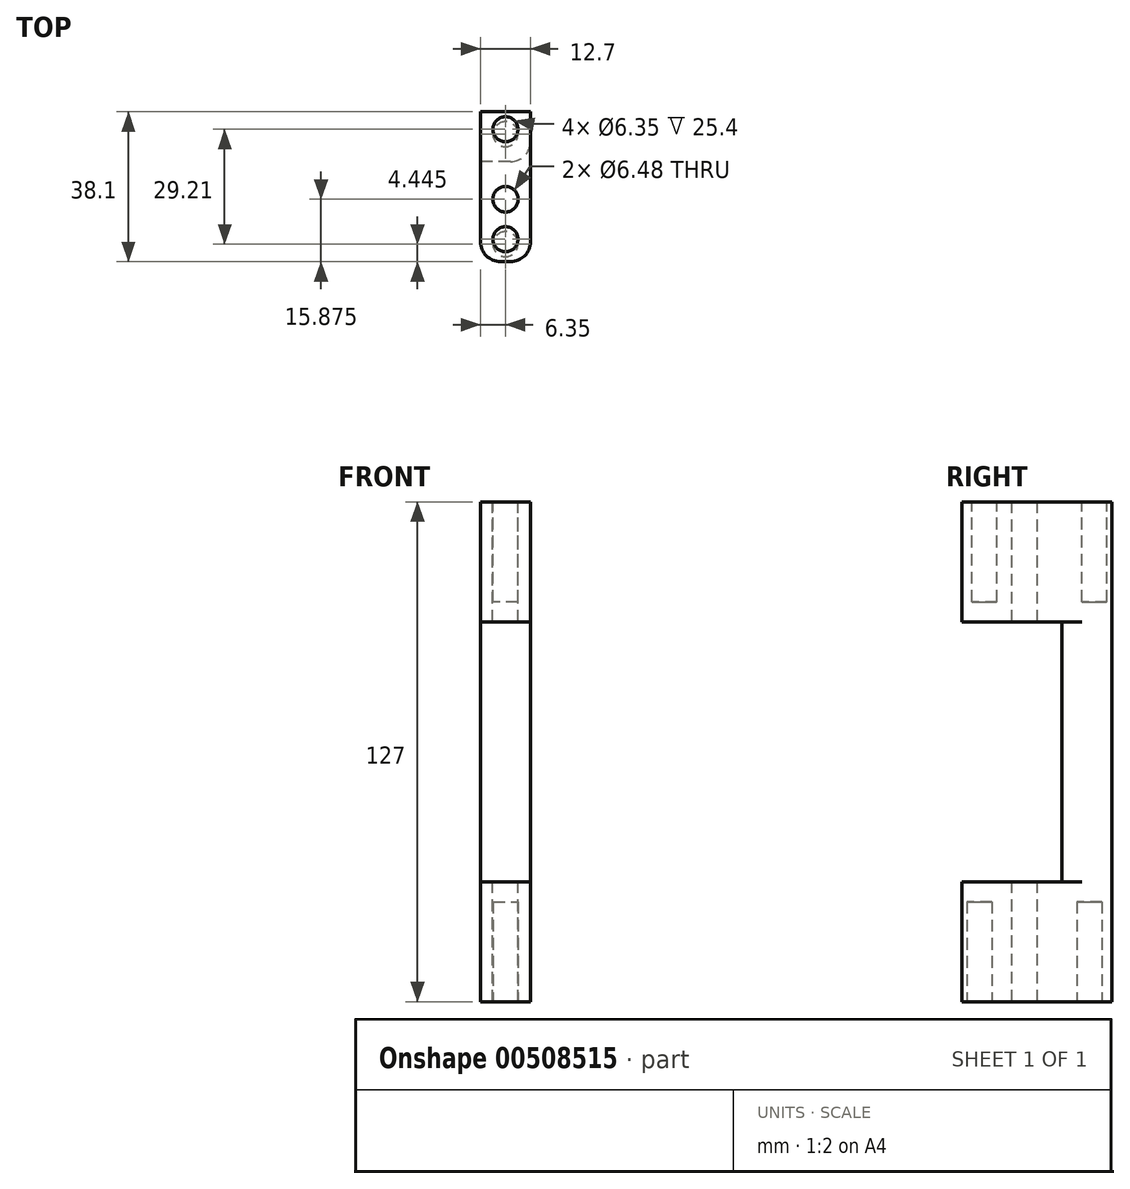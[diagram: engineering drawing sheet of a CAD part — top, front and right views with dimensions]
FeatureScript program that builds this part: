
annotation { "Feature Type Name" : "Feature", "Feature Type Description" : "" }
export const myFeature = defineFeature(function(context is Context, id is Id, definition is map)
    precondition{}
    {
        {
            var Q0;
            Q0=qCreatedBy(makeId("Top.planeOp"),FACE);
            var sketch = newSketch(context, id + "F0", { "sketchPlane" : qUnion([Q0])});
            skLineSegment(sketch, "E0.bottom", {"start": v(0, 0) * mm, "end": v(12.7, 0) * mm});
            skLineSegment(sketch, "E0.top", {"start": v(0, 38.1) * mm, "end": v(12.7, 38.1) * mm});
            skLineSegment(sketch, "E0.left", {"start": v(0, 0) * mm, "end": v(0, 38.1) * mm});
            skLineSegment(sketch, "E0.right", {"start": v(12.7, 0) * mm, "end": v(12.7, 38.1) * mm});
            skSolve(sketch);
        }
        {
            var Q0;
            Q0=makeQuery(id+"F0.imprint","IMPRINT",FACE,{"disambiguationData":[TD([[makeQuery(id+"F0.imprint","IMPRINT",EDGE,{"derivedFrom":sQuery(id+"F0.wireOp",EDGE,"E0.bottom")}),1.0]])]});
            extrude(context, id + "F1", {"entities" : qUnion([Q0]), "depth" : 127 * mm, "offsetDistance" : 25.4 * mm});
        }
        {
            var Q0;
            Q0=makeQuery(id+"F1.opExtrude","CAP_FACE",FACE,{"disambiguationData":[OSD([sQuery(id+"F0.wireOp",EDGE,"E0.bottom"),sQuery(id+"F0.wireOp",EDGE,"E0.top"),sQuery(id+"F0.wireOp",EDGE,"E0.left"),sQuery(id+"F0.wireOp",EDGE,"E0.right")])],"isStart":false});
            var sketch = newSketch(context, id + "F2", { "sketchPlane" : qUnion([Q0])});
            skCircle(sketch, "E1", {"center": v(6.35, 33.66) * mm, "radius": 3.18 * mm});
            skCircle(sketch, "E2", {"center": v(6.35, 5.71) * mm, "radius": 3.18 * mm});
            skLineSegment(sketch, "E3", {"start": v(0, 33.66) * mm, "end": v(12.7, 33.66) * mm, "construction": true});
            skLineSegment(sketch, "E4", {"start": v(0, 5.71) * mm, "end": v(12.7, 5.71) * mm, "construction": true});
            skLineSegment(sketch, "E5", {"start": v(0, 15.88) * mm, "end": v(12.7, 15.88) * mm, "construction": true});
            skCircle(sketch, "E6", {"center": v(6.35, 15.88) * mm, "radius": 3.24 * mm});
            skSolve(sketch);
        }
        {
            var Q0;
            Q0=makeQuery(id+"F2.imprint","IMPRINT",FACE,{"disambiguationData":[TD([[makeQuery(id+"F2.imprint","IMPRINT",EDGE,{"derivedFrom":sQuery(id+"F2.wireOp",EDGE,"E6")}),1.0]])]});
            extrude(context, id + "F3", {"entities" : qUnion([Q0]), "operationType" : NewBodyOperationType.REMOVE, "oppositeDirection" : true, "depth" : 152.4 * mm, "offsetDistance" : 25.4 * mm});
        }
        {
            var Q0;
            Q0=makeQuery(id+"F2.imprint","IMPRINT",FACE,{"disambiguationData":[TD([[makeQuery(id+"F2.imprint","IMPRINT",EDGE,{"derivedFrom":sQuery(id+"F2.wireOp",EDGE,"E1")}),1.0]])]});
            var Q1;
            Q1=makeQuery(id+"F2.imprint","IMPRINT",FACE,{"disambiguationData":[TD([[makeQuery(id+"F2.imprint","IMPRINT",EDGE,{"derivedFrom":sQuery(id+"F2.wireOp",EDGE,"E2")}),1.0]])]});
            extrude(context, id + "F4", {"entities" : qUnion([Q0, Q1]), "operationType" : NewBodyOperationType.REMOVE, "oppositeDirection" : true, "depth" : 25.4 * mm, "offsetDistance" : 25.4 * mm});
        }
        {
            var Q0;
            Q0=makeQuery(id+"F1.opExtrude","CAP_FACE",FACE,{"disambiguationData":[OSD([sQuery(id+"F0.wireOp",EDGE,"E0.bottom"),sQuery(id+"F0.wireOp",EDGE,"E0.top"),sQuery(id+"F0.wireOp",EDGE,"E0.left"),sQuery(id+"F0.wireOp",EDGE,"E0.right")])],"isStart":true});
            var sketch = newSketch(context, id + "F5", { "sketchPlane" : qUnion([Q0])});
            skCircle(sketch, "E7", {"center": v(6.35, -4.45) * mm, "radius": 3.18 * mm});
            skCircle(sketch, "E8", {"center": v(6.35, -32.39) * mm, "radius": 3.18 * mm});
            skLineSegment(sketch, "E9", {"start": v(0, -4.45) * mm, "end": v(12.7, -4.44) * mm, "construction": true});
            skLineSegment(sketch, "E10", {"start": v(0, -32.39) * mm, "end": v(12.7, -32.39) * mm, "construction": true});
            skSolve(sketch);
        }
        {
            var Q0;
            Q0=makeQuery(id+"F5.imprint","IMPRINT",FACE,{"disambiguationData":[TD([[makeQuery(id+"F5.imprint","IMPRINT",EDGE,{"derivedFrom":sQuery(id+"F5.wireOp",EDGE,"E7")}),1.0]])]});
            var Q1;
            Q1=makeQuery(id+"F5.imprint","IMPRINT",FACE,{"disambiguationData":[TD([[makeQuery(id+"F5.imprint","IMPRINT",EDGE,{"derivedFrom":sQuery(id+"F5.wireOp",EDGE,"E8")}),1.0]])]});
            extrude(context, id + "F6", {"entities" : qUnion([Q0, Q1]), "operationType" : NewBodyOperationType.REMOVE, "oppositeDirection" : true, "depth" : 25.4 * mm, "offsetDistance" : 25.4 * mm});
        }
        {
            var Q0;
            Q0=makeQuery(id+"F1.opExtrude","SWEPT_FACE",FACE,{"disambiguationData":[OSD([sQuery(id+"F0.wireOp",EDGE,"E0.left")])]});
            var sketch = newSketch(context, id + "F7", { "sketchPlane" : qUnion([Q0])});
            skLineSegment(sketch, "E11", {"start": v(0, 30.48) * mm, "end": v(-25.4, 30.48) * mm});
            skLineSegment(sketch, "E12", {"start": v(-25.4, 30.48) * mm, "end": v(-25.4, 96.52) * mm});
            skLineSegment(sketch, "E13", {"start": v(-25.4, 96.52) * mm, "end": v(0, 96.52) * mm});
            skSolve(sketch);
        }
        {
            var Q0;
            {var subQ0=sQuery(id+"F7.wireOp",EDGE,"E11");Q0=makeQuery(id+"F7.imprint","IMPRINT",FACE,{"disambiguationData":[TD([[makeQuery(id+"F7.imprint","IMPRINT",EDGE,{"derivedFrom":subQ0}),-1.0]])]});}
            extrude(context, id + "F8", {"entities" : qUnion([Q0]), "operationType" : NewBodyOperationType.REMOVE, "oppositeDirection" : true, "depth" : 25.4 * mm, "offsetDistance" : 25.4 * mm});
        }
        {
            var Q0;
            {var subQ0=sQuery(id+"F0.wireOp",EDGE,"E0.bottom");var subQ1=sQuery(id+"F0.wireOp",EDGE,"E0.right");Q0=makeQuery(id+"F8.boolean.opBoolean","SPLIT",EDGE,{"disambiguationData":[TD([makeQuery(id+"F8.opExtrude","SWEPT_FACE",FACE,{"disambiguationData":[OSD([sQuery(id+"F7.wireOp",EDGE,"E13")])]})])],"derivedFrom":makeQuery(id+"F1.opExtrude","SWEPT_EDGE",EDGE,{"disambiguationData":[OSD([subQ0,subQ1])]})});}
            var Q1;
            {var subQ0=sQuery(id+"F0.wireOp",EDGE,"E0.bottom");var subQ1=sQuery(id+"F0.wireOp",EDGE,"E0.left");Q1=makeQuery(id+"F8.boolean.opBoolean","SPLIT",EDGE,{"disambiguationData":[TD([makeQuery(id+"F8.opExtrude","SWEPT_FACE",FACE,{"disambiguationData":[OSD([sQuery(id+"F7.wireOp",EDGE,"E13")])]})])],"derivedFrom":makeQuery(id+"F1.opExtrude","SWEPT_EDGE",EDGE,{"disambiguationData":[OSD([subQ0,subQ1])]})});}
            var Q2;
            Q2=makeQuery(id+"F8.boolean.opBoolean","INTERSECT",EDGE,{"derivedFrom":[makeQuery(id+"F1.opExtrude","SWEPT_FACE",FACE,{"disambiguationData":[OSD([sQuery(id+"F0.wireOp",EDGE,"E0.right")])]}),makeQuery(id+"F8.opExtrude","SWEPT_FACE",FACE,{"disambiguationData":[OSD([sQuery(id+"F7.wireOp",EDGE,"E12")])]})]});
            var Q3;
            Q3=makeQuery(id+"F8.boolean.opBoolean","COPY",EDGE,{"derivedFrom":makeQuery(id+"F8.opExtrude","CAP_EDGE",EDGE,{"disambiguationData":[OSD([sQuery(id+"F7.wireOp",EDGE,"E12")])],"isStart":true})});
            var Q4;
            {var subQ0=sQuery(id+"F0.wireOp",EDGE,"E0.bottom");var subQ1=sQuery(id+"F0.wireOp",EDGE,"E0.right");Q4=makeQuery(id+"F8.boolean.opBoolean","SPLIT",EDGE,{"disambiguationData":[TD([makeQuery(id+"F8.opExtrude","SWEPT_FACE",FACE,{"disambiguationData":[OSD([sQuery(id+"F7.wireOp",EDGE,"E11")])]})])],"derivedFrom":makeQuery(id+"F1.opExtrude","SWEPT_EDGE",EDGE,{"disambiguationData":[OSD([subQ0,subQ1])]})});}
            var Q5;
            {var subQ0=sQuery(id+"F0.wireOp",EDGE,"E0.bottom");var subQ1=sQuery(id+"F0.wireOp",EDGE,"E0.left");Q5=makeQuery(id+"F8.boolean.opBoolean","SPLIT",EDGE,{"disambiguationData":[TD([makeQuery(id+"F8.opExtrude","SWEPT_FACE",FACE,{"disambiguationData":[OSD([sQuery(id+"F7.wireOp",EDGE,"E11")])]})])],"derivedFrom":makeQuery(id+"F1.opExtrude","SWEPT_EDGE",EDGE,{"disambiguationData":[OSD([subQ0,subQ1])]})});}
            fillet(context, id + "F9", {"entities" : qUnion([Q0, Q1, Q2, Q3, Q4, Q5]), "radius" : 5.08 * mm, "tangentPropagation" : true, "allowEdgeOverflow" : false});
        }
    });
